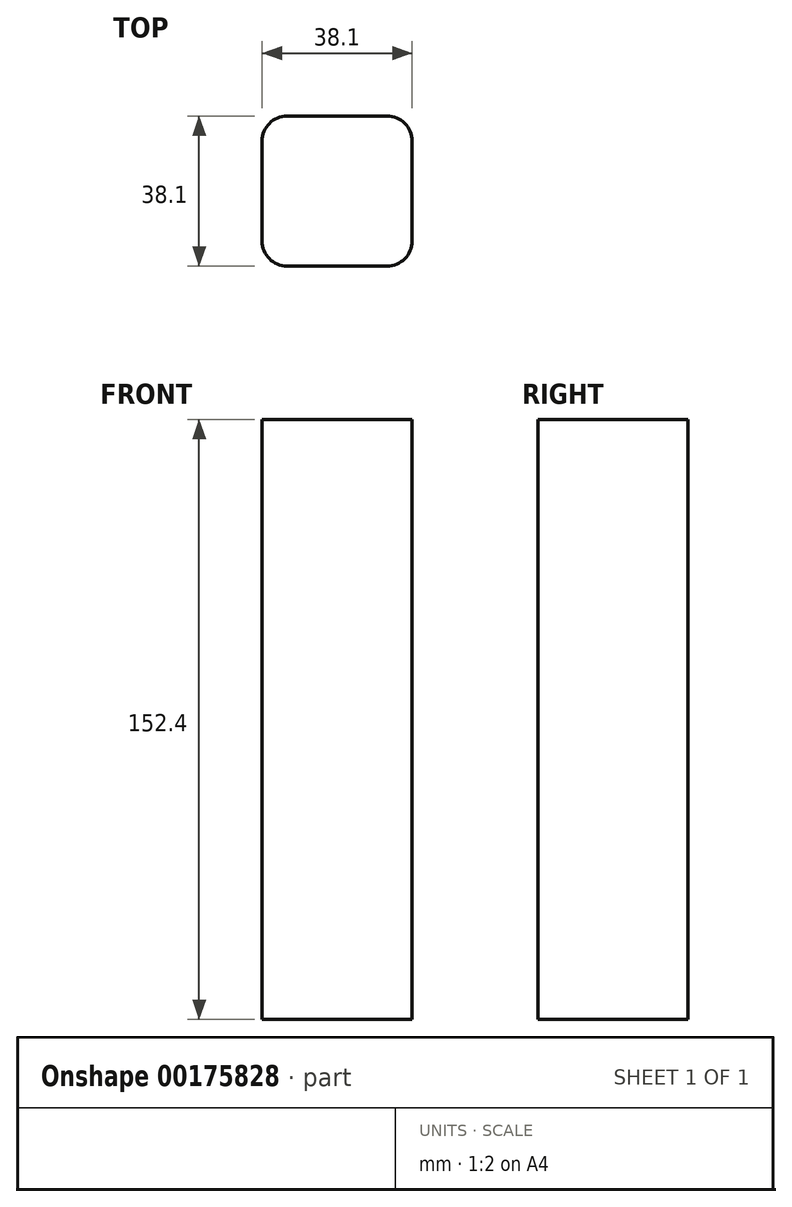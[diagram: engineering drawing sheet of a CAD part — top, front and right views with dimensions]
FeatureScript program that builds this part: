
annotation { "Feature Type Name" : "Feature", "Feature Type Description" : "" }
export const myFeature = defineFeature(function(context is Context, id is Id, definition is map)
    precondition{}
    {
        {
            var Q0;
            Q0=qCreatedBy(makeId("Top.planeOp"),FACE);
            var sketch = newSketch(context, id + "F0", { "sketchPlane" : qUnion([Q0])});
            skLineSegment(sketch, "E0.bottom", {"start": v(12.7, 19.05) * mm, "end": v(-12.7, 19.05) * mm});
            skLineSegment(sketch, "E0.top", {"start": v(12.7, -19.05) * mm, "end": v(-12.7, -19.05) * mm});
            skLineSegment(sketch, "E0.left", {"start": v(19.05, 12.7) * mm, "end": v(19.05, -12.7) * mm});
            skLineSegment(sketch, "E0.right", {"start": v(-19.05, 12.7) * mm, "end": v(-19.05, -12.7) * mm});
            skPoint(sketch, "E0.middle", {"position": v(0, 0) * mm});
            skPoint(sketch, "E1.visualSharp", {"position": v(-19.05, 19.05) * mm});
            skArc(sketch, "E1.filletArc", {"start": v(-12.7, 19.05) * mm, "mid": v(-17.2, 17.2) * mm, "end": v(-19.05, 12.7) * mm});
            skPoint(sketch, "E2.visualSharp", {"position": v(19.05, 19.05) * mm});
            skArc(sketch, "E2.filletArc", {"start": v(19.05, 12.7) * mm, "mid": v(17.2, 17.2) * mm, "end": v(12.7, 19.05) * mm});
            skPoint(sketch, "E3.visualSharp", {"position": v(19.05, -19.05) * mm});
            skArc(sketch, "E3.filletArc", {"start": v(12.7, -19.05) * mm, "mid": v(17.2, -17.2) * mm, "end": v(19.05, -12.7) * mm});
            skPoint(sketch, "E4.visualSharp", {"position": v(-19.05, -19.05) * mm});
            skArc(sketch, "E4.filletArc", {"start": v(-19.05, -12.7) * mm, "mid": v(-17.2, -17.2) * mm, "end": v(-12.7, -19.05) * mm});
            skSolve(sketch);
        }
        {
            var Q0;
            Q0=qSketchRegion(id+"F0",true);
            extrude(context, id + "F1", {"entities" : qUnion([Q0]), "depth" : 152.4 * mm, "offsetDistance" : 25.4 * mm});
        }
    });
